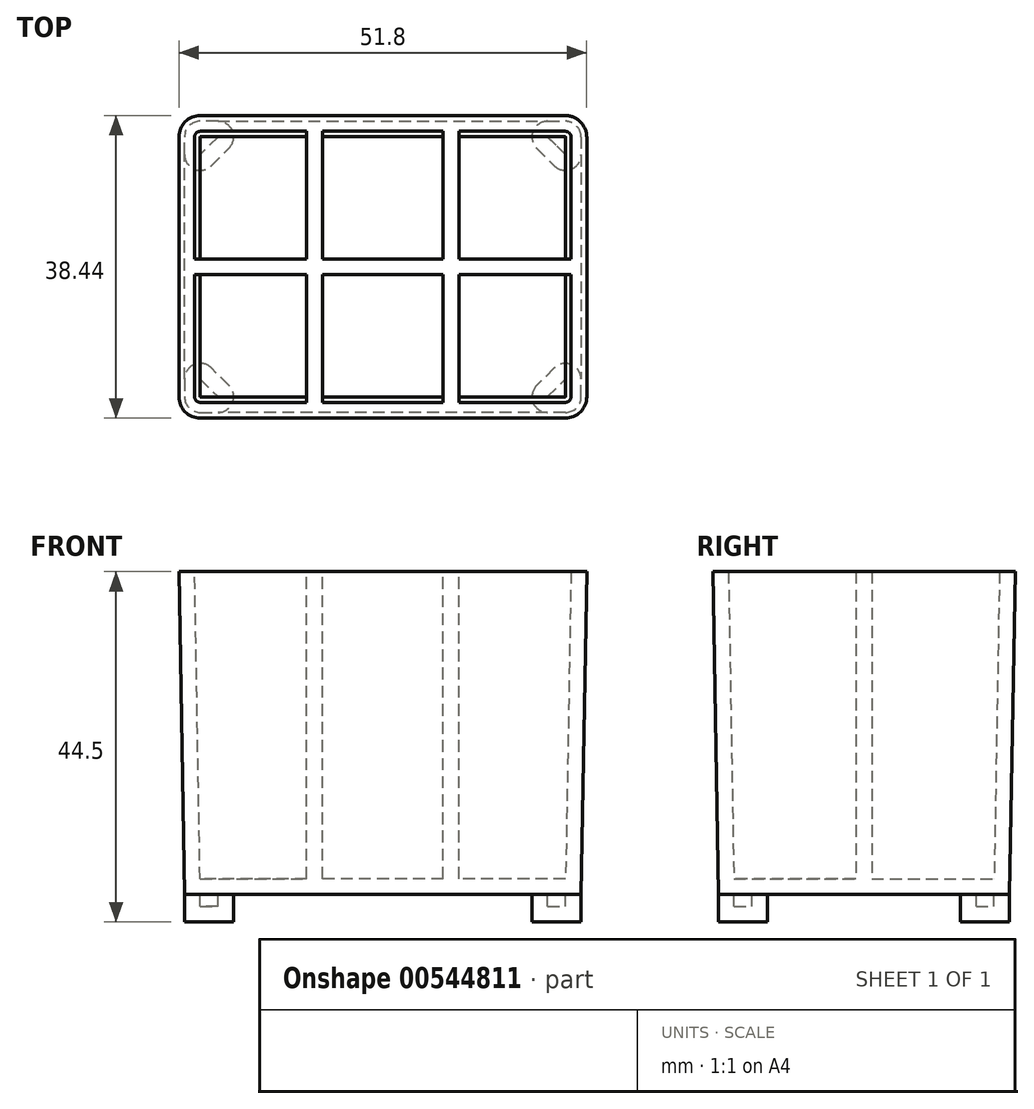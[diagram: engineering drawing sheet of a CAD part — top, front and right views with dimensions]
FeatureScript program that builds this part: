
annotation { "Feature Type Name" : "Feature", "Feature Type Description" : "" }
export const myFeature = defineFeature(function(context is Context, id is Id, definition is map)
    precondition{}
    {
        {
            var Q0;
            Q0=qCreatedBy(makeId("Top.planeOp"),FACE);
            var sketch = newSketch(context, id + "F0", { "sketchPlane" : qUnion([Q0])});
            skLineSegment(sketch, "E0.bottom", {"start": v(-20.94, 18.5) * mm, "end": v(-23.19, 18.5) * mm});
            skLineSegment(sketch, "E0.left", {"start": v(25.19, 16.5) * mm, "end": v(25.19, 14.26) * mm});
            skLineSegment(sketch, "E0.right", {"start": v(-25.19, -14.26) * mm, "end": v(-25.19, -16.5) * mm});
            skPoint(sketch, "E0.middle", {"position": v(0, 0) * mm});
            skPoint(sketch, "E1.visualSharp", {"position": v(-25.19, 18.5) * mm});
            skArc(sketch, "E1.filletArc", {"start": v(-23.19, 18.5) * mm, "mid": v(-24.6, 17.91) * mm, "end": v(-25.19, 16.5) * mm});
            skPoint(sketch, "E2.visualSharp", {"position": v(25.19, 18.5) * mm});
            skArc(sketch, "E2.filletArc", {"start": v(25.19, 16.5) * mm, "mid": v(24.6, 17.91) * mm, "end": v(23.19, 18.5) * mm});
            skPoint(sketch, "E3.visualSharp", {"position": v(25.19, -18.5) * mm});
            skArc(sketch, "E3.filletArc", {"start": v(23.19, -18.5) * mm, "mid": v(24.6, -17.91) * mm, "end": v(25.19, -16.5) * mm});
            skPoint(sketch, "E4.visualSharp", {"position": v(-25.19, -18.5) * mm});
            skLineSegment(sketch, "E5.0", {"start": v(-19.53, -15.09) * mm, "end": v(-21.77, -12.84) * mm});
            skLineSegment(sketch, "E6.0", {"start": v(-21.77, 12.84) * mm, "end": v(-19.53, 15.09) * mm});
            skLineSegment(sketch, "E7.0", {"start": v(21.77, -12.84) * mm, "end": v(19.53, -15.09) * mm});
            skLineSegment(sketch, "E8.0", {"start": v(19.53, 15.09) * mm, "end": v(21.77, 12.84) * mm});
            skPoint(sketch, "E9", {"position": v(-25.19, -9.43) * mm});
            skArc(sketch, "E10.filletArc", {"start": v(-21.77, -12.84) * mm, "mid": v(-23.95, -12.4) * mm, "end": v(-25.19, -14.26) * mm});
            skArc(sketch, "E11.filletArc", {"start": v(-20.94, -18.5) * mm, "mid": v(-19.1, -17.27) * mm, "end": v(-19.53, -15.09) * mm});
            skArc(sketch, "E12.filletArc", {"start": v(-19.53, 15.09) * mm, "mid": v(-19.1, 17.27) * mm, "end": v(-20.94, 18.5) * mm});
            skArc(sketch, "E13.filletArc", {"start": v(21.77, 12.84) * mm, "mid": v(23.95, 12.4) * mm, "end": v(25.19, 14.26) * mm});
            skLineSegment(sketch, "E14", {"start": v(20.94, 18.5) * mm, "end": v(23.19, 18.5) * mm});
            skLineSegment(sketch, "E15", {"start": v(25.19, -16.5) * mm, "end": v(25.19, -14.26) * mm});
            skLineSegment(sketch, "E16", {"start": v(23.19, -18.5) * mm, "end": v(20.94, -18.5) * mm});
            skLineSegment(sketch, "E17", {"start": v(-25.19, 14.26) * mm, "end": v(-25.19, 16.5) * mm});
            skArc(sketch, "E18.filletArc", {"start": v(-25.19, 14.26) * mm, "mid": v(-23.95, 12.4) * mm, "end": v(-21.77, 12.84) * mm});
            skArc(sketch, "E19.filletArc", {"start": v(19.53, -15.09) * mm, "mid": v(19.1, -17.27) * mm, "end": v(20.94, -18.5) * mm});
            skArc(sketch, "E20.filletArc", {"start": v(25.19, -14.26) * mm, "mid": v(23.95, -12.4) * mm, "end": v(21.77, -12.84) * mm});
            skArc(sketch, "E21.filletArc", {"start": v(20.94, 18.5) * mm, "mid": v(19.1, 17.27) * mm, "end": v(19.53, 15.09) * mm});
            skLineSegment(sketch, "E22", {"start": v(-20.94, 18.5) * mm, "end": v(20.94, 18.5) * mm});
            skLineSegment(sketch, "E23", {"start": v(25.19, 14.26) * mm, "end": v(25.19, -14.26) * mm});
            skLineSegment(sketch, "E24", {"start": v(20.94, -18.5) * mm, "end": v(-20.94, -18.5) * mm});
            skLineSegment(sketch, "E25", {"start": v(-25.19, 14.26) * mm, "end": v(-25.19, -14.26) * mm});
            skLineSegment(sketch, "E26", {"start": v(-23.19, -18.5) * mm, "end": v(-20.94, -18.5) * mm});
            skLineSegment(sketch, "E27", {"start": v(-23.19, -18.5) * mm, "end": v(-23.19, -18.5) * mm});
            skArc(sketch, "E28.filletArc", {"start": v(-25.19, -16.5) * mm, "mid": v(-24.6, -17.91) * mm, "end": v(-23.19, -18.5) * mm});
            skLineSegment(sketch, "E29.0", {"start": v(-25.19, 1) * mm, "end": v(-9.67, 1) * mm});
            skLineSegment(sketch, "E30.0", {"start": v(-25.19, -1) * mm, "end": v(-9.67, -1) * mm});
            skPoint(sketch, "E31.orphan", {"position": v(0, 18.5) * mm});
            skPoint(sketch, "E32.orphan", {"position": v(0, -18.5) * mm});
            skLineSegment(sketch, "E33.0", {"start": v(-9.67, 18.5) * mm, "end": v(-9.67, 1) * mm});
            skLineSegment(sketch, "E34.0", {"start": v(-7.67, 18.5) * mm, "end": v(-7.67, 1) * mm});
            skLineSegment(sketch, "E35.0", {"start": v(7.67, 18.5) * mm, "end": v(7.67, 1) * mm});
            skLineSegment(sketch, "E36.0", {"start": v(9.67, 18.5) * mm, "end": v(9.67, 1) * mm});
            skLineSegment(sketch, "E37.trimOffspring", {"start": v(-7.67, -1) * mm, "end": v(7.67, -1) * mm});
            skPoint(sketch, "E38.orphan", {"position": v(25.19, 0) * mm});
            skLineSegment(sketch, "E39.trimOffspring", {"start": v(7.67, -1) * mm, "end": v(7.67, -18.5) * mm});
            skLineSegment(sketch, "E40.trimOffspring", {"start": v(9.67, -1) * mm, "end": v(25.19, -1) * mm});
            skLineSegment(sketch, "E41.trimOffspring", {"start": v(-7.67, -1) * mm, "end": v(-7.67, -18.5) * mm});
            skLineSegment(sketch, "E42.trimOffspring", {"start": v(-9.67, -1) * mm, "end": v(-9.67, -18.5) * mm});
            skLineSegment(sketch, "E43.trimOffspring", {"start": v(-7.67, 1) * mm, "end": v(7.67, 1) * mm});
            skPoint(sketch, "E44.start.orphan", {"position": v(-25.19, 0) * mm});
            skLineSegment(sketch, "E45.trimOffspring", {"start": v(9.67, -1) * mm, "end": v(9.67, -18.5) * mm});
            skLineSegment(sketch, "E46.trimOffspring", {"start": v(9.67, 1) * mm, "end": v(25.19, 1) * mm});
            skSolve(sketch);
        }
        {
            var Q0;
            Q0=makeQuery(id+"F0.imprint","IMPRINT",FACE,{"disambiguationData":[TD([[makeQuery(id+"F0.imprint","IMPRINT",EDGE,{"derivedFrom":sQuery(id+"F0.wireOp",EDGE,"E0.bottom")}),1.0]])]});
            var Q1;
            Q1=makeQuery(id+"F0.imprint","IMPRINT",FACE,{"disambiguationData":[TD([[makeQuery(id+"F0.imprint","IMPRINT",EDGE,{"derivedFrom":sQuery(id+"F0.wireOp",EDGE,"E0.left")}),-1.0]])]});
            var Q2;
            Q2=makeQuery(id+"F0.imprint","IMPRINT",FACE,{"disambiguationData":[TD([[makeQuery(id+"F0.imprint","IMPRINT",EDGE,{"derivedFrom":sQuery(id+"F0.wireOp",EDGE,"E3.filletArc")}),1.0]])]});
            var Q3;
            Q3=makeQuery(id+"F0.imprint","IMPRINT",FACE,{"disambiguationData":[TD([[makeQuery(id+"F0.imprint","IMPRINT",EDGE,{"derivedFrom":sQuery(id+"F0.wireOp",EDGE,"E0.right")}),1.0]])]});
            extrude(context, id + "F1", {"entities" : qUnion([Q0, Q1, Q2, Q3]), "oppositeDirection" : true, "depth" : 3.5 * mm, "offsetDistance" : 25 * mm});
        }
        {
            var Q0;
            Q0 = qSketchRegion(id + "F0", true);
            var Q1;
            Q1=makeQuery(id+"F1.opExtrude","CAP_FACE",FACE,{"disambiguationData":[OSD([sQuery(id+"F0.wireOp",EDGE,"E0.right"),sQuery(id+"F0.wireOp",EDGE,"E5.0"),sQuery(id+"F0.wireOp",EDGE,"E10.filletArc"),sQuery(id+"F0.wireOp",EDGE,"E11.filletArc"),sQuery(id+"F0.wireOp",EDGE,"E26"),sQuery(id+"F0.wireOp",EDGE,"E28.filletArc")])],"isStart":true});
            extrude(context, id + "F2", {"entities" : qUnion([Q0, Q1]), "operationType" : NewBodyOperationType.ADD, "depth" : 41 * mm, "offsetDistance" : 25 * mm, "hasDraft" : true, "draftAngle" : 1 * degree});
        }
        {
            var Q0;
            Q0=makeQuery(id+"F2.opExtrude","CAP_FACE",FACE,{"disambiguationData":[OSD([sQuery(id+"F0.wireOp",EDGE,"E0.bottom"),sQuery(id+"F0.wireOp",EDGE,"E0.left"),sQuery(id+"F0.wireOp",EDGE,"E0.right"),sQuery(id+"F0.wireOp",EDGE,"E1.filletArc"),sQuery(id+"F0.wireOp",EDGE,"E2.filletArc"),sQuery(id+"F0.wireOp",EDGE,"E3.filletArc"),sQuery(id+"F0.wireOp",EDGE,"E14"),sQuery(id+"F0.wireOp",EDGE,"E15"),sQuery(id+"F0.wireOp",EDGE,"E16"),sQuery(id+"F0.wireOp",EDGE,"E17"),sQuery(id+"F0.wireOp",EDGE,"E22"),sQuery(id+"F0.wireOp",EDGE,"E23"),sQuery(id+"F0.wireOp",EDGE,"E24"),sQuery(id+"F0.wireOp",EDGE,"E25"),sQuery(id+"F0.wireOp",EDGE,"E26"),sQuery(id+"F0.wireOp",EDGE,"E28.filletArc")])],"isStart":false});
            shell(context, id + "F3", {"entities" : qUnion([Q0]), "thickness" : 2 * mm});
        }
        {
            var Q0;
            {var subQ2=sQuery(id+"F0.wireOp",EDGE,"E29.0");Q0=makeQuery(id+"F0.imprint","IMPRINT",FACE,{"disambiguationData":[TD([[makeQuery(id+"F0.imprint","IMPRINT",EDGE,{"derivedFrom":subQ2}),-1.0]])]});}
            extrude(context, id + "F4", {"entities" : qUnion([Q0]), "operationType" : NewBodyOperationType.ADD, "depth" : 41 * mm, "offsetDistance" : 25 * mm});
        }
        {
            var Q0;
            Q0=makeQuery(id+"F0.imprint","IMPRINT",FACE,{"disambiguationData":[TD([[makeQuery(id+"F0.imprint","IMPRINT",EDGE,{"derivedFrom":sQuery(id+"F0.wireOp",EDGE,"E0.bottom")}),1.0]])]});
            var Q1;
            Q1=makeQuery(id+"F0.imprint","IMPRINT",FACE,{"disambiguationData":[TD([[makeQuery(id+"F0.imprint","IMPRINT",EDGE,{"derivedFrom":sQuery(id+"F0.wireOp",EDGE,"E0.left")}),-1.0]])]});
            var Q2;
            Q2=makeQuery(id+"F0.imprint","IMPRINT",FACE,{"disambiguationData":[TD([[makeQuery(id+"F0.imprint","IMPRINT",EDGE,{"derivedFrom":sQuery(id+"F0.wireOp",EDGE,"E3.filletArc")}),1.0]])]});
            var Q3;
            Q3=makeQuery(id+"F0.imprint","IMPRINT",FACE,{"disambiguationData":[TD([[makeQuery(id+"F0.imprint","IMPRINT",EDGE,{"derivedFrom":sQuery(id+"F0.wireOp",EDGE,"E0.right")}),1.0]])]});
            extrude(context, id + "F5", {"entities" : qUnion([Q0, Q1, Q2, Q3]), "operationType" : NewBodyOperationType.ADD, "depth" : 2 * mm, "offsetDistance" : 25 * mm});
        }
    });
